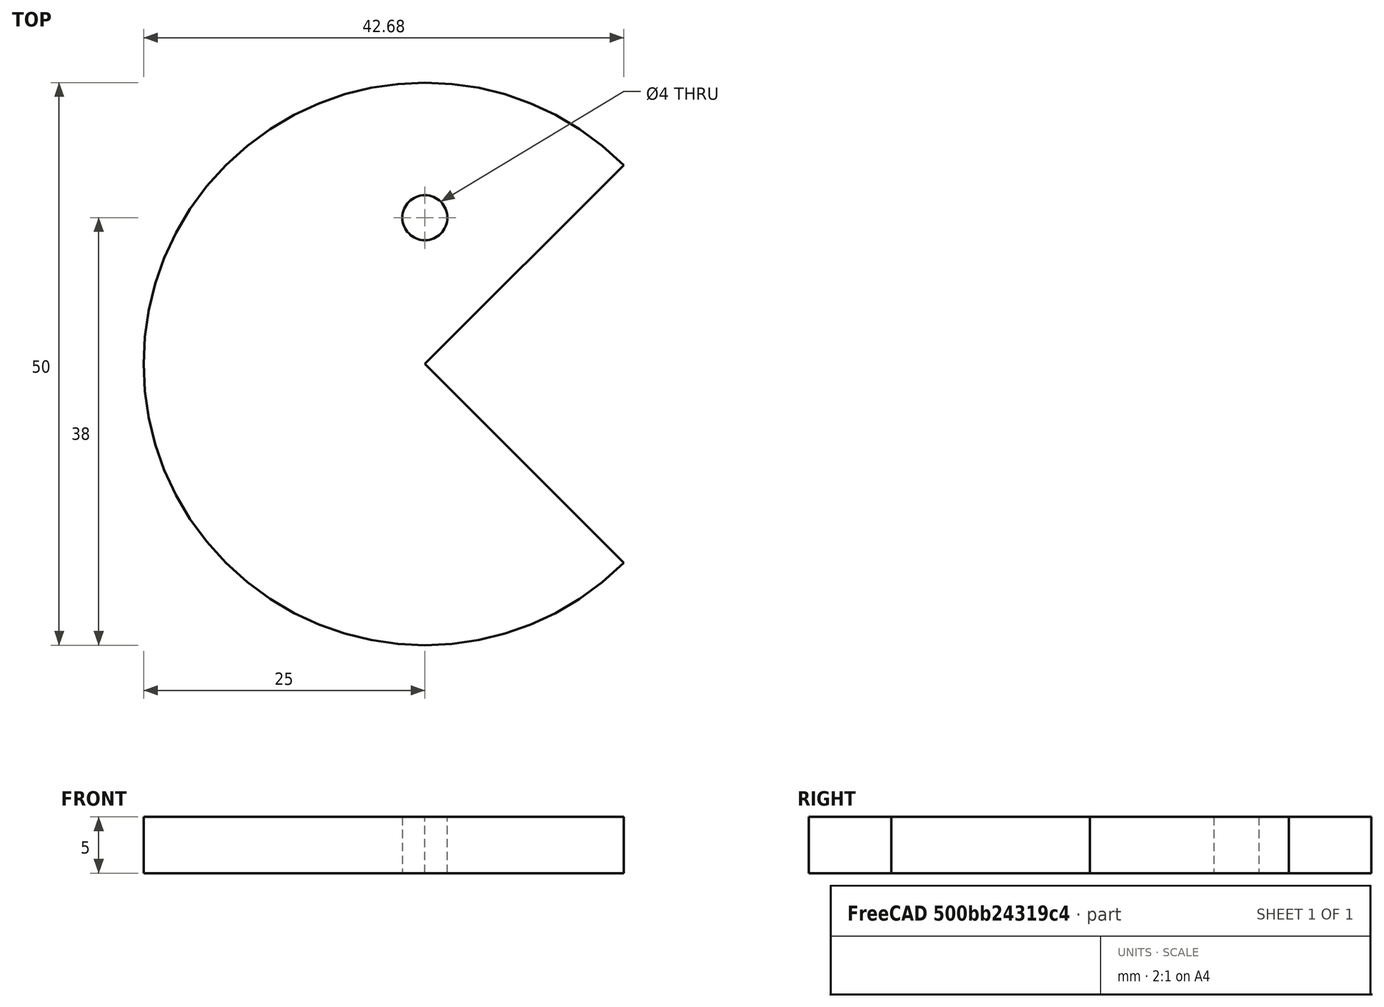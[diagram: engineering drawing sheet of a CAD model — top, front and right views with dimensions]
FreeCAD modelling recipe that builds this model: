
FCSTD DOCUMENT  (FreeCAD 1.0R39319 (Git))
Label: ojt1_t09p01_pacman
License: All rights reserved
LicenseURL: https://en.wikipedia.org/wiki/All_rights_reserved
objects: Part::Cylinder×2, PartDesign::Body×1, Part::Cut×1
note: 4 computed .brp shape members not serialized (recipe doc carries the construction recipe); baked Part::Feature solids carry a one-line shape summary decoded from their .brp

FEATURE [PartDesign::Body] Body  label="Cos"
  AllowCompound = false
  Origin = -> Origin
FEATURE [Part::Cylinder] Cylinder  label="cara_pacman"
  Angle = 270
  AttacherType = Attacher::AttachEngine3D
  FirstAngle = 0
  Height = 5
  Placement = pos=(0,0,0) rot=(0,0,1;0.785398rad)
  Radius = 25
  SecondAngle = 0
FEATURE [Part::Cylinder] Cylinder001  label="ull_pacman"
  Angle = 360
  AttacherType = Attacher::AttachEngine3D
  FirstAngle = 0
  Height = 10
  Placement = pos=(0,13,-2) rot=(0,0,1;0rad)
  Radius = 2
  SecondAngle = 0
FEATURE [Part::Cut] Cut  label="pacman"
  Base = -> Cylinder
  Tool = -> Cylinder001
